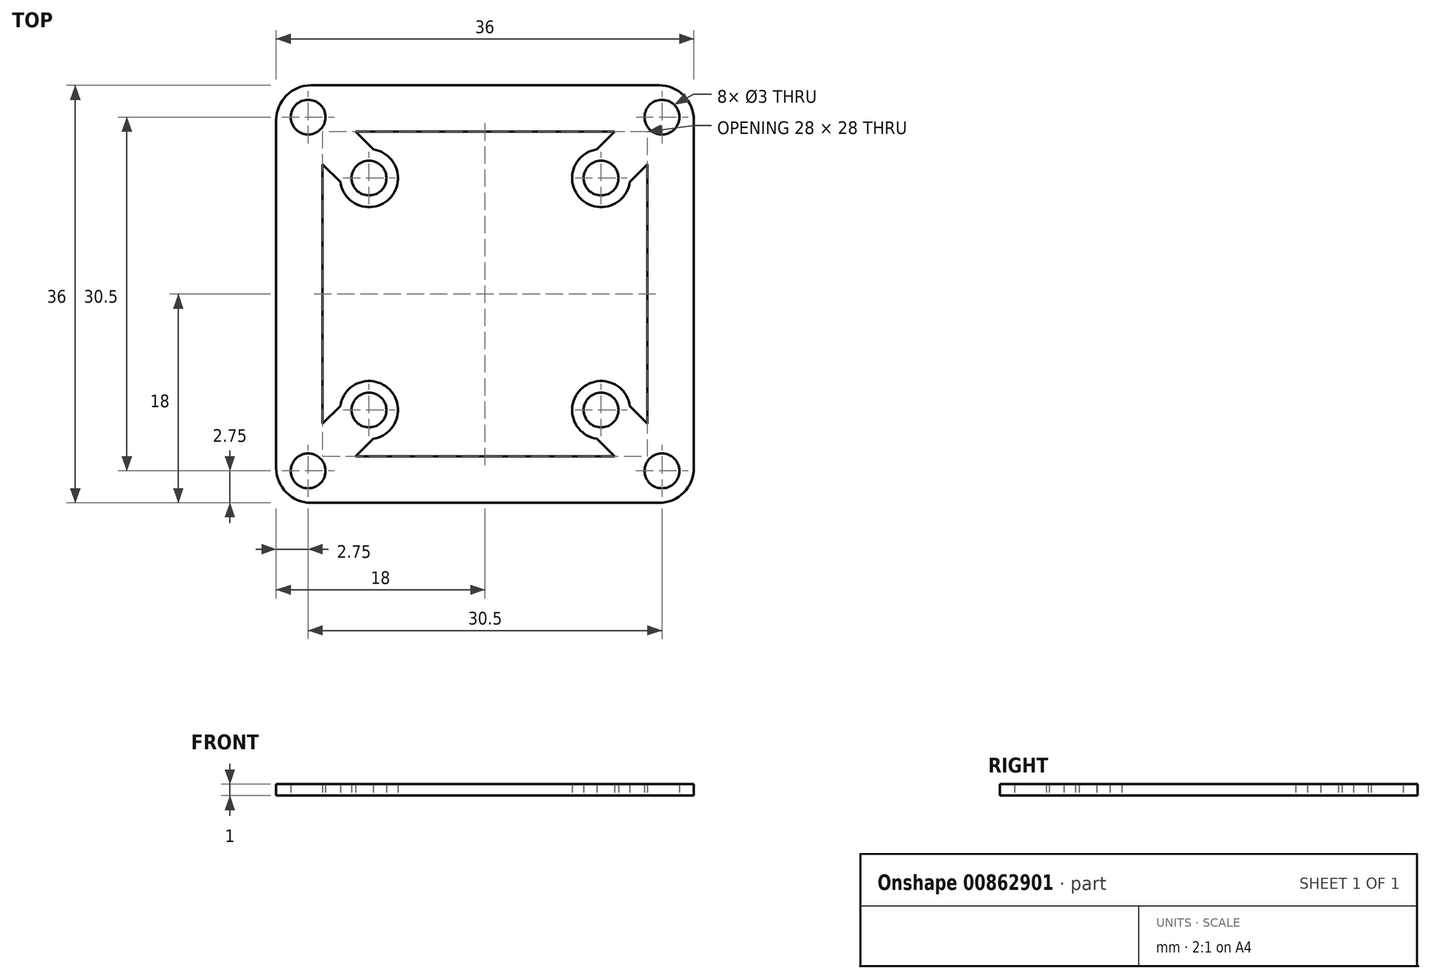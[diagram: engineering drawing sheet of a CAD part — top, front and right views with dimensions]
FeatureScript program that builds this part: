
annotation { "Feature Type Name" : "Feature", "Feature Type Description" : "" }
export const myFeature = defineFeature(function(context is Context, id is Id, definition is map)
    precondition{}
    {
        {
            var Q0;
            Q0=qCreatedBy(makeId("Top.planeOp"),FACE);
            var sketch = newSketch(context, id + "F0", { "sketchPlane" : qUnion([Q0])});
            skCircle(sketch, "E0", {"center": v(-10, 10) * mm, "radius": 1.5 * mm});
            skCircle(sketch, "E1.0.1.0", {"center": v(-10, -10) * mm, "radius": 1.5 * mm});
            skCircle(sketch, "E1.1.0.0", {"center": v(10, 10) * mm, "radius": 1.5 * mm});
            skCircle(sketch, "E1.1.1.0", {"center": v(10, -10) * mm, "radius": 1.5 * mm});
            skLineSegment(sketch, "E1.direction1", {"start": v(-10, 10) * mm, "end": v(10, 10) * mm, "construction": true});
            skLineSegment(sketch, "E1.direction2", {"start": v(-10, 10) * mm, "end": v(-10, -10) * mm, "construction": true});
            skCircle(sketch, "E2", {"center": v(-15.25, 15.25) * mm, "radius": 1.5 * mm});
            skCircle(sketch, "E3.0.1.0", {"center": v(-15.25, -15.25) * mm, "radius": 1.5 * mm});
            skCircle(sketch, "E3.1.0.0", {"center": v(15.25, 15.25) * mm, "radius": 1.5 * mm});
            skCircle(sketch, "E3.1.1.0", {"center": v(15.25, -15.25) * mm, "radius": 1.5 * mm});
            skLineSegment(sketch, "E3.direction1", {"start": v(-15.25, 15.25) * mm, "end": v(15.25, 15.25) * mm, "construction": true});
            skLineSegment(sketch, "E3.direction2", {"start": v(-15.25, 15.25) * mm, "end": v(-15.25, -15.25) * mm, "construction": true});
            skLineSegment(sketch, "E4.bottom", {"start": v(-15, 18) * mm, "end": v(15, 18) * mm});
            skLineSegment(sketch, "E4.top", {"start": v(-15, -18) * mm, "end": v(15, -18) * mm});
            skLineSegment(sketch, "E4.left", {"start": v(-18, 15) * mm, "end": v(-18, -15) * mm});
            skLineSegment(sketch, "E4.right", {"start": v(18, 15) * mm, "end": v(18, -15) * mm});
            skPoint(sketch, "E4.middle", {"position": v(0, 0) * mm});
            skLineSegment(sketch, "E5.bottom", {"start": v(14, -14) * mm, "end": v(-14, -14) * mm});
            skLineSegment(sketch, "E5.top", {"start": v(14, 14) * mm, "end": v(-14, 14) * mm});
            skLineSegment(sketch, "E5.left", {"start": v(14, -14) * mm, "end": v(14, 14) * mm});
            skLineSegment(sketch, "E5.right", {"start": v(-14, -14) * mm, "end": v(-14, 14) * mm});
            skCircle(sketch, "E6", {"center": v(-10, 10) * mm, "radius": 2.5 * mm});
            skCircle(sketch, "E7.0.1.0", {"center": v(-10, -10) * mm, "radius": 2.5 * mm});
            skCircle(sketch, "E7.1.0.0", {"center": v(10, 10) * mm, "radius": 2.5 * mm});
            skCircle(sketch, "E7.1.1.0", {"center": v(10, -10) * mm, "radius": 2.5 * mm});
            skPoint(sketch, "E8.visualSharp", {"position": v(-18, -18) * mm});
            skArc(sketch, "E8.filletArc", {"start": v(-18, -15) * mm, "mid": v(-17.12, -17.12) * mm, "end": v(-15, -18) * mm});
            skPoint(sketch, "E9.visualSharp", {"position": v(18, -18) * mm});
            skArc(sketch, "E9.filletArc", {"start": v(15, -18) * mm, "mid": v(17.12, -17.12) * mm, "end": v(18, -15) * mm});
            skPoint(sketch, "E10.visualSharp", {"position": v(18, 18) * mm});
            skArc(sketch, "E10.filletArc", {"start": v(18, 15) * mm, "mid": v(17.12, 17.12) * mm, "end": v(15, 18) * mm});
            skPoint(sketch, "E11.visualSharp", {"position": v(-18, 18) * mm});
            skArc(sketch, "E11.filletArc", {"start": v(-15, 18) * mm, "mid": v(-17.12, 17.12) * mm, "end": v(-18, 15) * mm});
            skLineSegment(sketch, "E12", {"start": v(15.25, 15.25) * mm, "end": v(10, 10) * mm});
            skLineSegment(sketch, "E13", {"start": v(-15.25, 15.25) * mm, "end": v(-10, 10) * mm});
            skLineSegment(sketch, "E14.0", {"start": v(13.84, 16.66) * mm, "end": v(8.59, 11.41) * mm});
            skLineSegment(sketch, "E15.0", {"start": v(16.66, 13.84) * mm, "end": v(11.41, 8.59) * mm});
            skLineSegment(sketch, "E16.0", {"start": v(-16.66, 13.84) * mm, "end": v(-11.41, 8.59) * mm});
            skLineSegment(sketch, "E17.0", {"start": v(-13.84, 16.66) * mm, "end": v(-8.59, 11.41) * mm});
            skLineSegment(sketch, "E18", {"start": v(-10, -10) * mm, "end": v(-15.25, -15.25) * mm});
            skLineSegment(sketch, "E19.0", {"start": v(-11.41, -8.59) * mm, "end": v(-16.66, -13.84) * mm});
            skLineSegment(sketch, "E20.0", {"start": v(-8.59, -11.41) * mm, "end": v(-13.84, -16.66) * mm});
            skLineSegment(sketch, "E21", {"start": v(10, -10) * mm, "end": v(15.25, -15.25) * mm});
            skLineSegment(sketch, "E22.0", {"start": v(8.59, -11.41) * mm, "end": v(13.84, -16.66) * mm});
            skLineSegment(sketch, "E23.0", {"start": v(11.41, -8.59) * mm, "end": v(16.66, -13.84) * mm});
            skSolve(sketch);
        }
        {
            var Q0;
            Q0 = qSketchRegion(id + "F0", true);
            var Q1;
            {var subQ0=sQuery(id+"F0.wireOp",EDGE,"E13");var subQ5=sQuery(id+"F0.wireOp",EDGE,"E6");var subQ6=makeQuery(id+"F0.imprint","INTERSECT",VERTEX,{"derivedFrom":[subQ5,subQ0]});Q1=makeQuery(id+"F0.imprint","IMPRINT",FACE,{"disambiguationData":[TD([[makeQuery(id+"F0.imprint","IMPRINT",EDGE,{"disambiguationData":[TD([[subQ6,1.0]])],"derivedFrom":subQ5}),-1.0]])]});}
            var Q2;
            {var subQ0=sQuery(id+"F0.wireOp",EDGE,"E13");var subQ5=sQuery(id+"F0.wireOp",EDGE,"E6");var subQ6=makeQuery(id+"F0.imprint","INTERSECT",VERTEX,{"derivedFrom":[subQ5,subQ0]});Q2=makeQuery(id+"F0.imprint","IMPRINT",FACE,{"disambiguationData":[TD([[makeQuery(id+"F0.imprint","IMPRINT",EDGE,{"disambiguationData":[TD([[subQ6,-1.0]])],"derivedFrom":subQ5}),-1.0]])]});}
            var Q3;
            Q3=makeQuery(id+"F0.imprint","IMPRINT",FACE,{"disambiguationData":[TD([[makeQuery(id+"F0.imprint","IMPRINT",EDGE,{"derivedFrom":sQuery(id+"F0.wireOp",EDGE,"E0")}),-1.0]])]});
            var Q4;
            {var subQ3=sQuery(id+"F0.wireOp",EDGE,"E14.0");var subQ5=sQuery(id+"F0.wireOp",EDGE,"E7.1.0.0");var subQ6=makeQuery(id+"F0.imprint","INTERSECT",VERTEX,{"derivedFrom":[subQ5,subQ3]});Q4=makeQuery(id+"F0.imprint","IMPRINT",FACE,{"disambiguationData":[TD([[makeQuery(id+"F0.imprint","IMPRINT",EDGE,{"disambiguationData":[TD([[subQ6,1.0]])],"derivedFrom":subQ5}),-1.0]])]});}
            var Q5;
            {var subQ0=sQuery(id+"F0.wireOp",EDGE,"E12");var subQ5=sQuery(id+"F0.wireOp",EDGE,"E7.1.0.0");var subQ6=makeQuery(id+"F0.imprint","INTERSECT",VERTEX,{"derivedFrom":[subQ5,subQ0]});Q5=makeQuery(id+"F0.imprint","IMPRINT",FACE,{"disambiguationData":[TD([[makeQuery(id+"F0.imprint","IMPRINT",EDGE,{"disambiguationData":[TD([[subQ6,1.0]])],"derivedFrom":subQ5}),-1.0]])]});}
            var Q6;
            Q6=makeQuery(id+"F0.imprint","IMPRINT",FACE,{"disambiguationData":[TD([[makeQuery(id+"F0.imprint","IMPRINT",EDGE,{"derivedFrom":sQuery(id+"F0.wireOp",EDGE,"E1.1.0.0")}),-1.0]])]});
            var Q7;
            {var subQ3=sQuery(id+"F0.wireOp",EDGE,"E23.0");var subQ5=sQuery(id+"F0.wireOp",EDGE,"E7.1.1.0");var subQ6=makeQuery(id+"F0.imprint","INTERSECT",VERTEX,{"derivedFrom":[subQ5,subQ3]});Q7=makeQuery(id+"F0.imprint","IMPRINT",FACE,{"disambiguationData":[TD([[makeQuery(id+"F0.imprint","IMPRINT",EDGE,{"disambiguationData":[TD([[subQ6,1.0]])],"derivedFrom":subQ5}),-1.0]])]});}
            var Q8;
            {var subQ3=sQuery(id+"F0.wireOp",EDGE,"E22.0");var subQ5=sQuery(id+"F0.wireOp",EDGE,"E7.1.1.0");var subQ6=makeQuery(id+"F0.imprint","INTERSECT",VERTEX,{"derivedFrom":[subQ5,subQ3]});Q8=makeQuery(id+"F0.imprint","IMPRINT",FACE,{"disambiguationData":[TD([[makeQuery(id+"F0.imprint","IMPRINT",EDGE,{"disambiguationData":[TD([[subQ6,-1.0]])],"derivedFrom":subQ5}),-1.0]])]});}
            var Q9;
            Q9=makeQuery(id+"F0.imprint","IMPRINT",FACE,{"disambiguationData":[TD([[makeQuery(id+"F0.imprint","IMPRINT",EDGE,{"derivedFrom":sQuery(id+"F0.wireOp",EDGE,"E1.1.1.0")}),-1.0]])]});
            var Q10;
            Q10=makeQuery(id+"F0.imprint","IMPRINT",FACE,{"disambiguationData":[TD([[makeQuery(id+"F0.imprint","IMPRINT",EDGE,{"derivedFrom":sQuery(id+"F0.wireOp",EDGE,"E1.0.1.0")}),-1.0]])]});
            var Q11;
            {var subQ0=sQuery(id+"F0.wireOp",EDGE,"E18");var subQ5=sQuery(id+"F0.wireOp",EDGE,"E7.0.1.0");var subQ6=makeQuery(id+"F0.imprint","INTERSECT",VERTEX,{"derivedFrom":[subQ5,subQ0]});Q11=makeQuery(id+"F0.imprint","IMPRINT",FACE,{"disambiguationData":[TD([[makeQuery(id+"F0.imprint","IMPRINT",EDGE,{"disambiguationData":[TD([[subQ6,1.0]])],"derivedFrom":subQ5}),-1.0]])]});}
            var Q12;
            {var subQ0=sQuery(id+"F0.wireOp",EDGE,"E18");var subQ5=sQuery(id+"F0.wireOp",EDGE,"E7.0.1.0");var subQ6=makeQuery(id+"F0.imprint","INTERSECT",VERTEX,{"derivedFrom":[subQ5,subQ0]});Q12=makeQuery(id+"F0.imprint","IMPRINT",FACE,{"disambiguationData":[TD([[makeQuery(id+"F0.imprint","IMPRINT",EDGE,{"disambiguationData":[TD([[subQ6,-1.0]])],"derivedFrom":subQ5}),-1.0]])]});}
            extrude(context, id + "F1", {"entities" : qUnion([Q0, Q1, Q2, Q3, Q4, Q5, Q6, Q7, Q8, Q9, Q10, Q11, Q12]), "depth" : 1 * mm, "offsetDistance" : 25 * mm});
        }
    });
